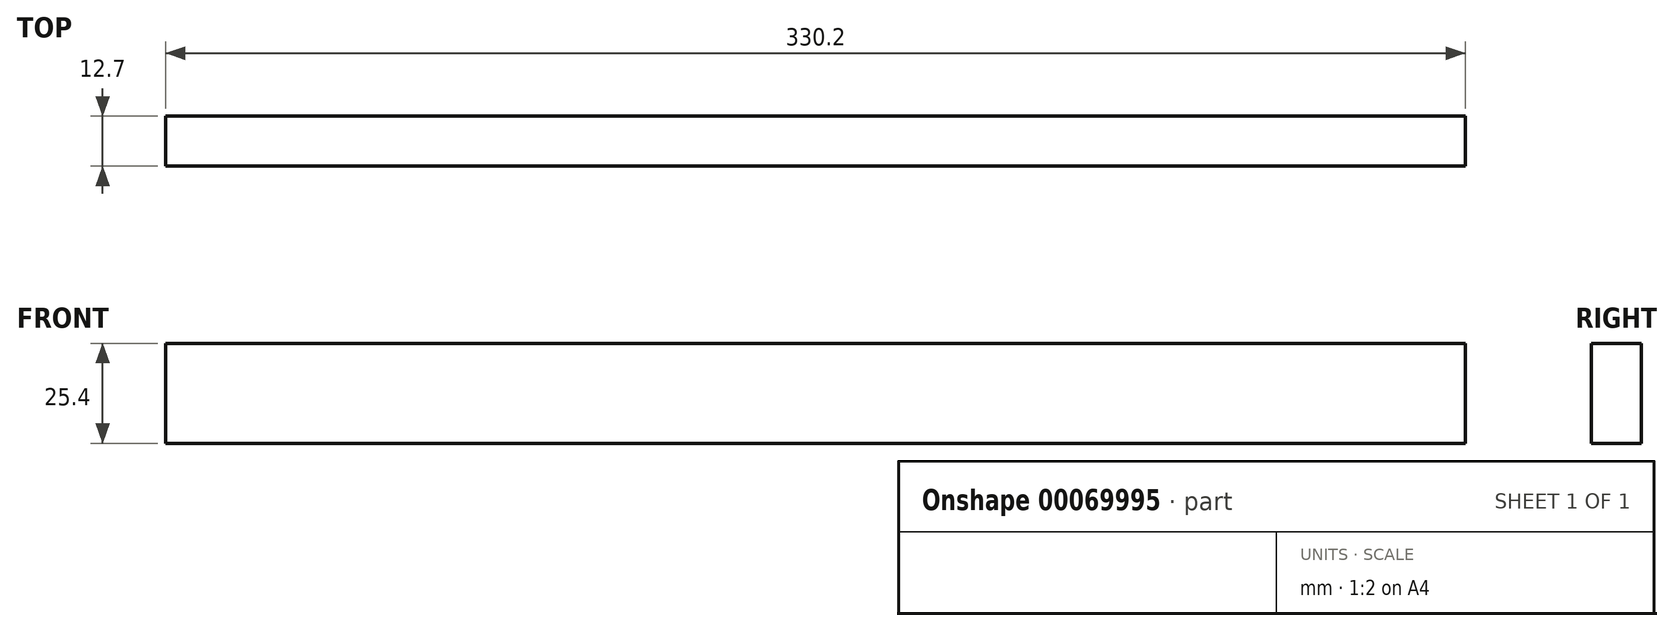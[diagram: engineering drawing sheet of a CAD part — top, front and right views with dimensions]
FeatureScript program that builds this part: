
annotation { "Feature Type Name" : "Feature", "Feature Type Description" : "" }
export const myFeature = defineFeature(function(context is Context, id is Id, definition is map)
    precondition{}
    {
        {
            var Q0;
            Q0=qCreatedBy(makeId("Front.planeOp"),FACE);
            var sketch = newSketch(context, id + "F0", { "sketchPlane" : qUnion([Q0])});
            skLineSegment(sketch, "E0.rect.bottom", {"start": v(165.1, 12.7) * mm, "end": v(-165.1, 12.7) * mm});
            skLineSegment(sketch, "E0.rect.top", {"start": v(165.1, -12.7) * mm, "end": v(-165.1, -12.7) * mm});
            skLineSegment(sketch, "E0.rect.left", {"start": v(165.1, 12.7) * mm, "end": v(165.1, -12.7) * mm});
            skLineSegment(sketch, "E0.rect.right", {"start": v(-165.1, 12.7) * mm, "end": v(-165.1, -12.7) * mm});
            skPoint(sketch, "E0.rect.middle", {"position": v(0, 0) * mm});
            skLineSegment(sketch, "E1", {"start": v(0, 12.7) * mm, "end": v(0, -12.7) * mm, "construction": true});
            skSolve(sketch);
        }
        {
            var Q0;
            Q0=makeQuery(id+"F0.imprint","IMPRINT",FACE,{"disambiguationData":[TD([[makeQuery(id+"F0.imprint","IMPRINT",EDGE,{"derivedFrom":sQuery(id+"F0.wireOp",EDGE,"abd1e121-c28f-4105-937f-708772ba65bf.bottom")}),1.0]])]});
            var Q1;
            {var subQ3=sQuery(id+"F0.wireOp",EDGE,"E0.rect.bottom");Q1=makeQuery(id+"F0.imprint","IMPRINT",FACE,{"disambiguationData":[TD([[makeQuery(id+"F0.imprint","IMPRINT",EDGE,{"derivedFrom":subQ3}),1.0]])]});}
            var Q2;
            Q2=makeQuery(id+"F0.imprint","IMPRINT",FACE,{"disambiguationData":[TD([[makeQuery(id+"F0.imprint","IMPRINT",EDGE,{"derivedFrom":sQuery(id+"F0.wireOp",EDGE,"98e05f21-933e-4f51-9880-0251b27cb64b0.MirrorCS")}),-1.0]])]});
            extrude(context, id + "F1", {"entities" : qUnion([Q0, Q1, Q2]), "depth" : 12.7 * mm});
        }
    });
